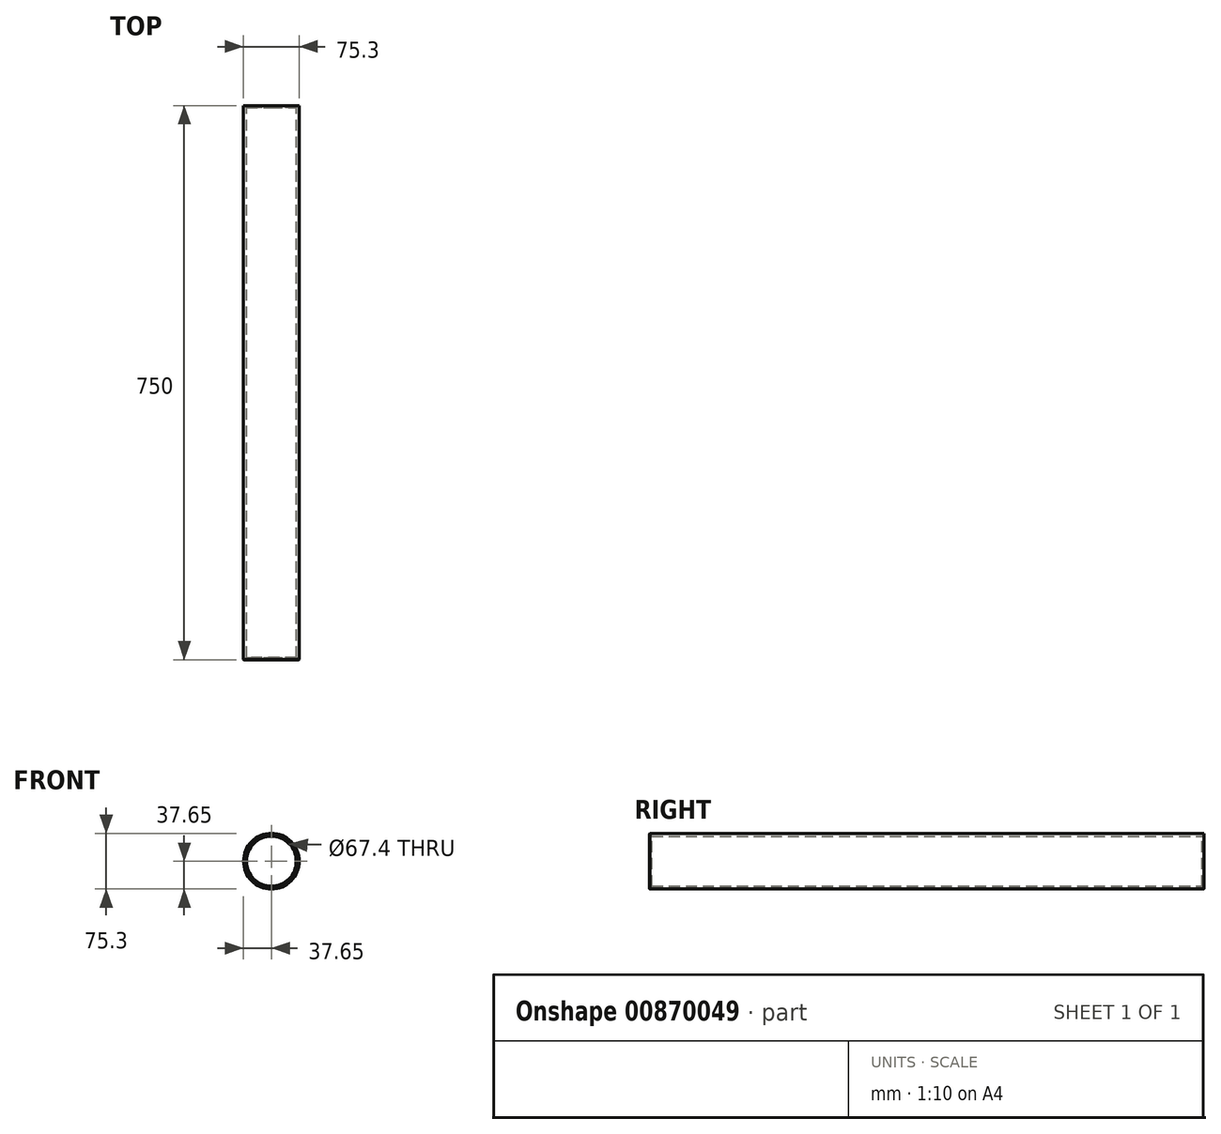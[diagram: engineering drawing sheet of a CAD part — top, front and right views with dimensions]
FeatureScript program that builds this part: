
annotation { "Feature Type Name" : "Feature", "Feature Type Description" : "" }
export const myFeature = defineFeature(function(context is Context, id is Id, definition is map)
    precondition{}
    {
        {
            var Q0;
            Q0=qCreatedBy(makeId("Front.planeOp"),FACE);
            var sketch = newSketch(context, id + "F0", { "sketchPlane" : qUnion([Q0])});
            skCircle(sketch, "E0", {"center": v(0, 0) * mm, "radius": 37.65 * mm});
            skCircle(sketch, "E1", {"center": v(0, 0) * mm, "radius": 33.7 * mm});
            skSolve(sketch);
        }
        {
            var Q0;
            Q0 = qSketchRegion(id + "F0", true);
            extrude(context, id + "F1", {"entities" : qUnion([Q0]), "endBound" : BoundingType.SYMMETRIC, "depth" : 750 * mm, "offsetDistance" : 25.4 * mm});
        }
        {
            var Q0;
            Q0=makeQuery(id+"F1.opExtrude","CAP_EDGE",EDGE,{"disambiguationData":[OSD([sQuery(id+"F0.wireOp",EDGE,"E1")])],"isStart":false});
            var Q1;
            Q1=makeQuery(id+"F1.opExtrude","CAP_EDGE",EDGE,{"disambiguationData":[OSD([sQuery(id+"F0.wireOp",EDGE,"E1")])],"isStart":true});
            chamfer(context, id + "F2", {"entities" : qUnion([Q0, Q1]), "chamferType" : ChamferType.OFFSET_ANGLE, "width" : 3 * mm, "oppositeDirection" : false, "angle" : 15 * degree, "tangentPropagation" : true});
        }
        {
            var Q0;
            Q0=makeQuery(id+"F1.opExtrude","CAP_EDGE",EDGE,{"disambiguationData":[OSD([sQuery(id+"F0.wireOp",EDGE,"E0")])],"isStart":false});
            var Q1;
            Q1=makeQuery(id+"F1.opExtrude","CAP_EDGE",EDGE,{"disambiguationData":[OSD([sQuery(id+"F0.wireOp",EDGE,"E0")])],"isStart":true});
            chamfer(context, id + "F3", {"entities" : qUnion([Q0, Q1]), "width" : 0.5 * mm, "tangentPropagation" : true});
        }
    });
